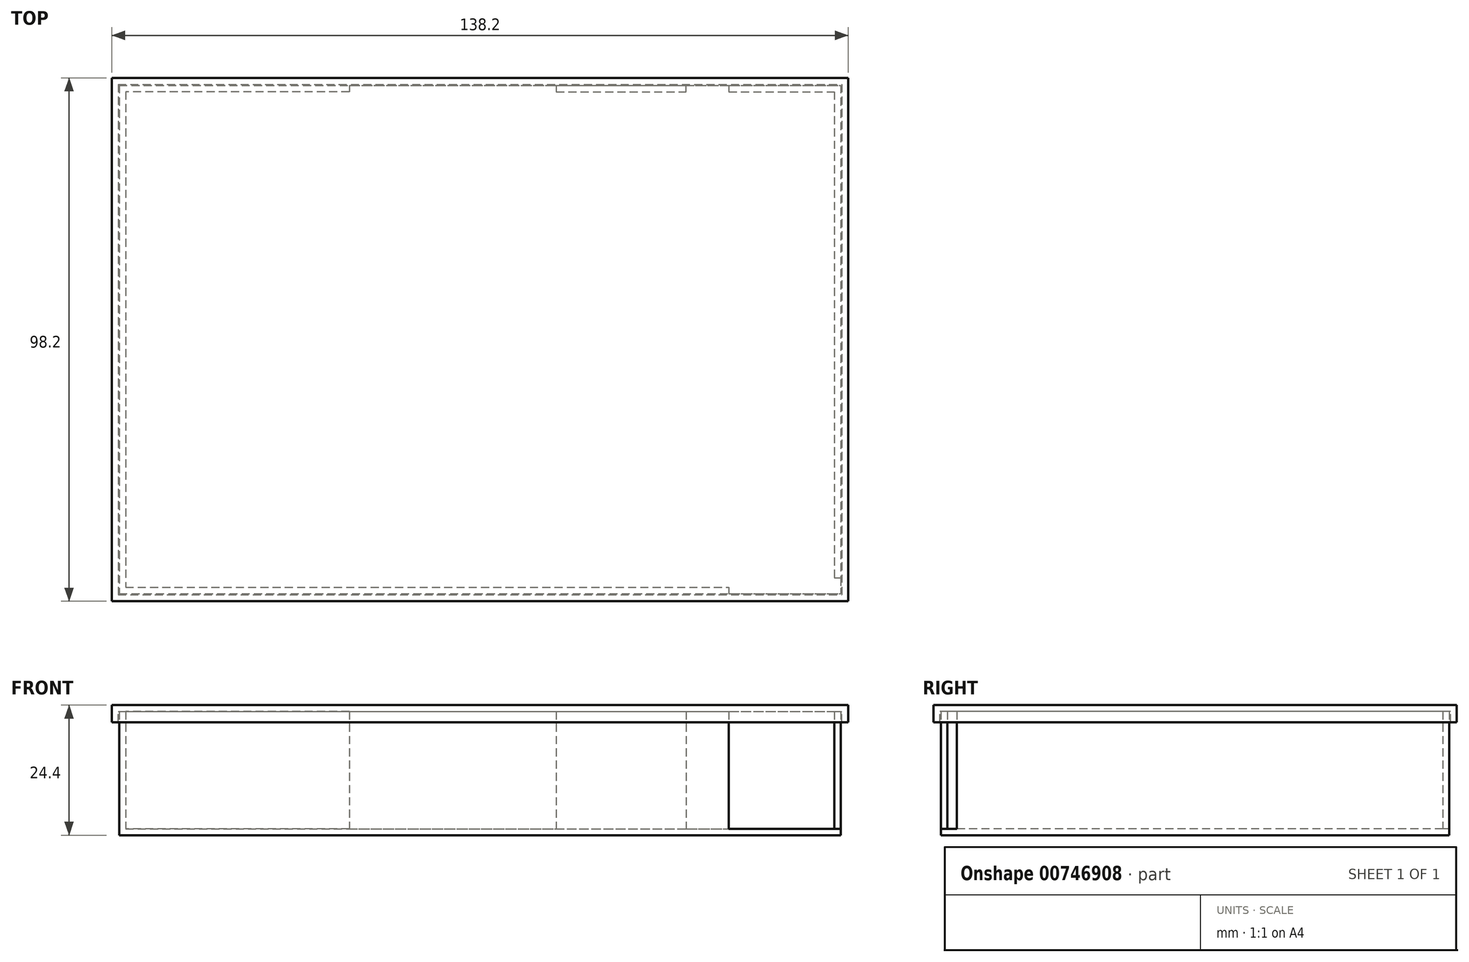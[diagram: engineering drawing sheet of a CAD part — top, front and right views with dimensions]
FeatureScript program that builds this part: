
annotation { "Feature Type Name" : "Feature", "Feature Type Description" : "" }
export const myFeature = defineFeature(function(context is Context, id is Id, definition is map)
    precondition{}
    {
        {
            var Q0;
            Q0=qCreatedBy(makeId("Top.planeOp"),FACE);
            var sketch = newSketch(context, id + "F0", { "sketchPlane" : qUnion([Q0])});
            skLineSegment(sketch, "E0.bottom", {"start": v(0, 0) * mm, "end": v(135.4, 0) * mm});
            skLineSegment(sketch, "E0.top", {"start": v(0, -95.4) * mm, "end": v(135.4, -95.4) * mm});
            skLineSegment(sketch, "E0.left", {"start": v(0, 0) * mm, "end": v(0, -95.4) * mm});
            skLineSegment(sketch, "E0.right", {"start": v(135.4, 0) * mm, "end": v(135.4, -95.4) * mm});
            skSolve(sketch);
        }
        {
            var Q0;
            Q0 = qSketchRegion(id + "F0", true);
            extrude(context, id + "F1", {"entities" : qUnion([Q0]), "depth" : 1.2 * mm, "offsetDistance" : 25 * mm});
        }
        {
            var Q0;
            Q0=makeQuery(id+"F1.opExtrude","CAP_FACE",FACE,{"disambiguationData":[OSD([sQuery(id+"F0.wireOp",EDGE,"E0.bottom"),sQuery(id+"F0.wireOp",EDGE,"E0.top"),sQuery(id+"F0.wireOp",EDGE,"E0.left"),sQuery(id+"F0.wireOp",EDGE,"E0.right")])],"isStart":false});
            var sketch = newSketch(context, id + "F2", { "sketchPlane" : qUnion([Q0])});
            skLineSegment(sketch, "E1", {"start": v(114.4, -95.4) * mm, "end": v(0, -95.4) * mm});
            skLineSegment(sketch, "E2", {"start": v(0, -95.4) * mm, "end": v(0, 0) * mm});
            skLineSegment(sketch, "E3", {"start": v(0, 0) * mm, "end": v(43.2, 0) * mm});
            skLineSegment(sketch, "E4", {"start": v(43.2, 0) * mm, "end": v(43.2, -1.2) * mm});
            skLineSegment(sketch, "E5", {"start": v(43.2, -1.2) * mm, "end": v(1.2, -1.2) * mm});
            skLineSegment(sketch, "E6", {"start": v(1.2, -1.2) * mm, "end": v(1.2, -94.2) * mm});
            skLineSegment(sketch, "E7", {"start": v(1.2, -94.2) * mm, "end": v(114.4, -94.2) * mm});
            skLineSegment(sketch, "E8", {"start": v(114.4, -94.2) * mm, "end": v(114.4, -95.4) * mm});
            skLineSegment(sketch, "E9", {"start": v(82, 0) * mm, "end": v(82, -1.2) * mm});
            skLineSegment(sketch, "E10", {"start": v(82, -1.2) * mm, "end": v(106.4, -1.2) * mm});
            skLineSegment(sketch, "E11", {"start": v(106.4, -1.2) * mm, "end": v(106.4, 0) * mm});
            skLineSegment(sketch, "E12", {"start": v(106.4, 0) * mm, "end": v(82, 0) * mm});
            skLineSegment(sketch, "E13", {"start": v(114.4, 0) * mm, "end": v(114.4, -1.2) * mm});
            skLineSegment(sketch, "E14", {"start": v(114.4, -1.2) * mm, "end": v(134.2, -1.2) * mm});
            skLineSegment(sketch, "E15", {"start": v(134.2, -1.2) * mm, "end": v(134.2, -92.4) * mm});
            skLineSegment(sketch, "E16", {"start": v(134.2, -92.4) * mm, "end": v(135.4, -92.4) * mm});
            skLineSegment(sketch, "E17", {"start": v(135.4, -92.4) * mm, "end": v(135.4, 0) * mm});
            skLineSegment(sketch, "E18", {"start": v(135.4, 0) * mm, "end": v(114.4, 0) * mm});
            skSolve(sketch);
        }
        {
            var Q0;
            Q0 = qSketchRegion(id + "F2", true);
            extrude(context, id + "F3", {"entities" : qUnion([Q0]), "operationType" : NewBodyOperationType.ADD, "depth" : 22 * mm, "offsetDistance" : 25 * mm});
        }
        {
            var Q0;
            Q0=makeQuery(id+"F3.opExtrude","CAP_FACE",FACE,{"disambiguationData":[OSD([sQuery(id+"F2.wireOp",EDGE,"E1"),sQuery(id+"F2.wireOp",EDGE,"E2"),sQuery(id+"F2.wireOp",EDGE,"E3"),sQuery(id+"F2.wireOp",EDGE,"E4"),sQuery(id+"F2.wireOp",EDGE,"E5"),sQuery(id+"F2.wireOp",EDGE,"E6"),sQuery(id+"F2.wireOp",EDGE,"E7"),sQuery(id+"F2.wireOp",EDGE,"E8")])],"isStart":false});
            var sketch = newSketch(context, id + "F4", { "sketchPlane" : qUnion([Q0])});
            skLineSegment(sketch, "E19.bottom", {"start": v(-1.4, 1.4) * mm, "end": v(136.8, 1.4) * mm});
            skLineSegment(sketch, "E19.top", {"start": v(-1.4, -96.8) * mm, "end": v(136.8, -96.8) * mm});
            skLineSegment(sketch, "E19.left", {"start": v(-1.4, 1.4) * mm, "end": v(-1.4, -96.8) * mm});
            skLineSegment(sketch, "E19.right", {"start": v(136.8, 1.4) * mm, "end": v(136.8, -96.8) * mm});
            skSolve(sketch);
        }
        {
            var Q0;
            Q0 = qSketchRegion(id + "F4", true);
            extrude(context, id + "F5", {"entities" : qUnion([Q0]), "depth" : 1.2 * mm, "offsetDistance" : 25 * mm});
        }
        {
            var Q0;
            Q0=makeQuery(id+"F4.imprint","IMPRINT",FACE,{"disambiguationData":[TD([[makeQuery(id+"F4.imprint","IMPRINT",EDGE,{"derivedFrom":sQuery(id+"F4.wireOp",EDGE,"E19.bottom")}),-1.0]])]});
            var sketch = newSketch(context, id + "F6", { "sketchPlane" : qUnion([Q0])});
            skLineSegment(sketch, "E20.0", {"start": v(-1.4, -96.8) * mm, "end": v(136.8, -96.8) * mm});
            skLineSegment(sketch, "E20.1", {"start": v(136.8, 1.4) * mm, "end": v(136.8, -96.8) * mm});
            skLineSegment(sketch, "E20.2", {"start": v(-1.4, 1.4) * mm, "end": v(136.8, 1.4) * mm});
            skLineSegment(sketch, "E20.3", {"start": v(-1.4, 1.4) * mm, "end": v(-1.4, -96.8) * mm});
            skLineSegment(sketch, "E21.0", {"start": v(135.6, 0.2) * mm, "end": v(135.6, -95.6) * mm});
            skLineSegment(sketch, "E21.1", {"start": v(-0.2, 0.2) * mm, "end": v(135.6, 0.2) * mm});
            skLineSegment(sketch, "E21.2", {"start": v(-0.2, 0.2) * mm, "end": v(-0.2, -95.6) * mm});
            skLineSegment(sketch, "E21.3", {"start": v(-0.2, -95.6) * mm, "end": v(135.6, -95.6) * mm});
            skSolve(sketch);
        }
        {
            var Q0;
            Q0 = qSketchRegion(id + "F6", true);
            extrude(context, id + "F7", {"entities" : qUnion([Q0]), "operationType" : NewBodyOperationType.ADD, "oppositeDirection" : true, "depth" : 2 * mm, "offsetDistance" : 25 * mm});
        }
    });
